# Revit family: Table-LAMMHULTS-CARGO-Trolley
name_source: partatom
category: Furniture
revit_build: Autodesk Revit 2015 (Build: 20160512_0715(x64)
units: mm (PartAtom-declared; Revit-internal decimal feet)

## types (2) — shared parameters
Assembly Code = E2020
Description = *Please enter mtrl description here for use in mto*
Frame Material = Metal - Chrome - Polished
Handle Material = Leather - Rustical - Brown
Height = 700 mm  [stored 2.29659 ft]
Keynote = 46.B
Length = 840 mm  [stored 2.75591 ft]
Manufacturer = LAMMHULTS
Model = CARGO
URL = www.lammhults.se
Weight = 17.5 Kg
Width = 350 mm  [stored 1.14829 ft]

## per-type parameters (varying)
| type | Shelves Material | Top Shelve Material |
| Glass | Glass-Frosted | Glass-Frosted |
| Laminate - White | Laminate - Compact - White | Laminate - Compact - White |

note: [stored X ft] marks values corroborated as IEEE doubles in the binary element streams (Revit-internal decimal feet)

## geometry (parser evidence)
native form markers: Blend x12, Sweep x3
no freeform markers — native parametric forms only
